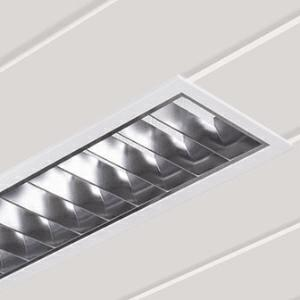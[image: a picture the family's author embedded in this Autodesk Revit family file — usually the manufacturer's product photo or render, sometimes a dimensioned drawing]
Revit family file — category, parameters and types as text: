
# Revit family: 3f_filippi_-_l_560_2s_3f_filippi_-_270937_-_l_562x12w_led_2s_221x647
name_source: partatom
category: Lighting Fixtures
units: mm (PartAtom-declared; Revit-internal decimal feet)

## family parameters
Cut with Voids When Loaded = No
Host = Face
Light Source = No
Part Type = Normal
Room Calculation Point = No
Round Connector Dimension = Use Diameter
Shared = No

## types (1)
- 3F Filippi - L 560 2S (1 x LED, 2937 lm, 28 W, 4000 K)
    Apparent Load = 28 VA
    Approval mark = ENEC
    CIE Flux Codes = 77 98 100 100 100
    Color Rendering = 80
    Color Temperature = 4000 K
    Control Gear = Electronic ballast
    Default Elevation = 1800 mm
    Description = ILLUMINOTECHNICAL
Luminous efficiency 100% (DLOR 100%, ULOR 0%).
Initial luminous flux of the luminaire 2937 lm.
Direct symmetric distribution.
Installation Interdistance Transv.D = 0.95 x hu - Long.D = 1.08 x hu.
Average luminance <1500 cd/m² for radial angles >65°.
Tabular UGR (CIE 117 - 4H-8H; S=0.25H; 70/50/20): RUG 15.7 - 18.
Beam angle: 62° - 78°.
Luminous efficacy 105 lm/W.
Lifetime (L93/B10): 30000 h. (tq+25°C)
Lifetime (L90/B10): 50000 h. (tq+25°C)
Lifetime (L85/B10): 80000 h. (tq+25°C)
Lifetime (L80/B10): 100000 h. (tq+25°C)
Sudden decreased luminous flux after 50000 hours: 0% (C0).
Photobiological safety in compliance with IEC/TR 62778: RG0 risk exempt, (IEC 62471).
In compliance with IEC/EN 62722-2-1 - IEC/EN 62717 standards.

SOURCE
2 linear LED modules 12W/840.
Energy efficiency class (UE 2019/2020 - UE 2019/2015): D.
CIE 13.3 Colour rendering index: CRI >80 (R9 <50%).
IES TM-30 Fidelity Index: Rf = 84 Rg = 95.
CCT nominal colour temperature 4000 K.
Colour initial tolerance (MacAdam): SDCM 3.

MECHANICAL
Housing in galvannealed steel, painted in white epoxy-polyester.
2S parabolic louvre in semi-specular aluminium, non-reflecting, with transverse blades closed at the top.
Prismatic flat diffuser in transparent methacrylate (PMMA), multilenticular, anti-glare, prismatic exterior, placed above louvre blades.
Film protective against dust and finger marks, adhesive, attached to louvre.
Luminaire with limited surface temperature. - D - (EN 60598-2-24)
Dimensions: 647x221 mm, height 95 mm. Weight 2.59 kg.
IP20 protection degree.
Mechanical strength to impacts IK02 (0.2 joule).
Glow-wire test resistance 650°C.

ELECTRICAL
Halogen Free electronic wiring 230V-50/60Hz, power factor 0.90, THD <25%, constant output current, SELV, class I, 1 driver.
Power of the luminaire 28 W.
CE - IEC 60598-1 - EN 60598-1.
SAFE FLICKER: PstLM=<1 and SVM=<0.4 (IEC TR 61547-1 and IEC TR 63158), to ensure a more comfortable and safe light.
Luminaire compliant with EN 60598-2-22 for power supply from a centralised emergency system CPSS (Central Power Supply System), not incorporated in the luminaire - high risk areas excluded. The default power and flux are 100% in AC and 100% in DC.
Ambient temperature from 0°C to +25°C.
Temperature class T6 max 85°C.
Relative humidity UR: <85%.

INSTALLATION
Pull-up recessed fitting / Slat ceiling recessed fitting.
False ceiling carving: 190x620 mm.
All accessories dedicated to this product are available on the Catalog and on our website www.3F-Filippi.com.

APPLICATIONS
In environments with VDTs, managerial offices and staterooms, public offices and schools.

WARNING
Luminaire designed for disposal/recycling at end-of-life.
Replaceable (LED only) light source by a professional. Replaceable control gear by a professional.
    Height = 0 mm  [stored 0 ft]
    Lamp = 1 x LED
    Lamp Light Flux = 2937 lm
    Lamp Power = 28 W
    Lamp count = 1
    Length = 647 mm
    Lifetime = 50000 h
    Luminous efficacy = 105 lm/W
    Manufacturer = 3F Filippi
    ModVariant = No
    Model = 3F Filippi - 270937 - L 562x12W LED 2S 221x647
    Mounting Place = Ceiling
    Mounting Type = Recessed
    Number of Poles = 1
    OnlyDefault = Yes
    Power Factor = 1
    Product Name = 3F Filippi - L 560 2S
    Product group = recessed luminaire
    ProductGroupID = 4
    Protection Class = Protection class I
    Protection Degree = IP 20
    RLX_Detail_Level = 1
    RLX_Emergency_Light_Flux = 0 lm
    RLX_Emergency_Type = 0
    RLX_Emergency_Type_DB = No
    RlxData = <blob elided: 59757 chars, md5=d5f39934>
    Socket = socket
    Standby Power = 0 W
    System Light Flux = 2937 lm
    System Power = 28 W
    Type Comments = Product without accessories
    Type Image = 3ffilippi_270937.jpg
    URL = http://relux.com
    VarID = ---
    Voltage = 0 V
    Weight = 0.00 kg
    Width = 221 mm

note: [stored X ft] marks values corroborated as IEEE doubles in the binary element streams (Revit-internal decimal feet)

## geometry (parser evidence)
native form markers: Blend x4, Sweep x10
no freeform markers — native parametric forms only
